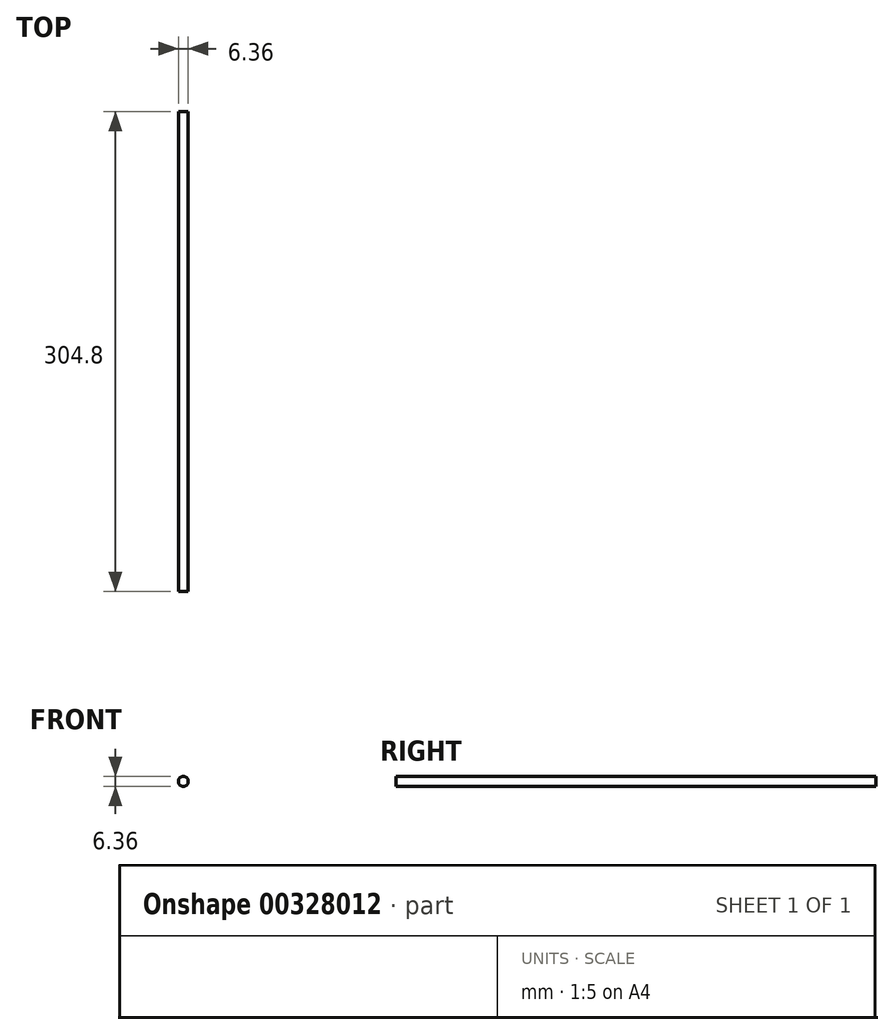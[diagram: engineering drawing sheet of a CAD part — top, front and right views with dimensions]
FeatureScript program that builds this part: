
annotation { "Feature Type Name" : "Feature", "Feature Type Description" : "" }
export const myFeature = defineFeature(function(context is Context, id is Id, definition is map)
    precondition{}
    {
        {
            var Q0;
            Q0=qCreatedBy(makeId("Front.planeOp"),FACE);
            var sketch = newSketch(context, id + "F0", { "sketchPlane" : qUnion([Q0])});
            skCircle(sketch, "E0", {"center": v(0, 0) * mm, "radius": 3.18 * mm});
            skSolve(sketch);
        }
        {
            var Q0;
            Q0=makeQuery(id+"F0.imprint","IMPRINT",FACE,{"disambiguationData":[TD([[makeQuery(id+"F0.imprint","IMPRINT",EDGE,{"derivedFrom":sQuery(id+"F0.wireOp",EDGE,"E0")}),1.0]])]});
            extrude(context, id + "F1", {"entities" : qUnion([Q0]), "depth" : 304.8 * mm});
        }
    });
